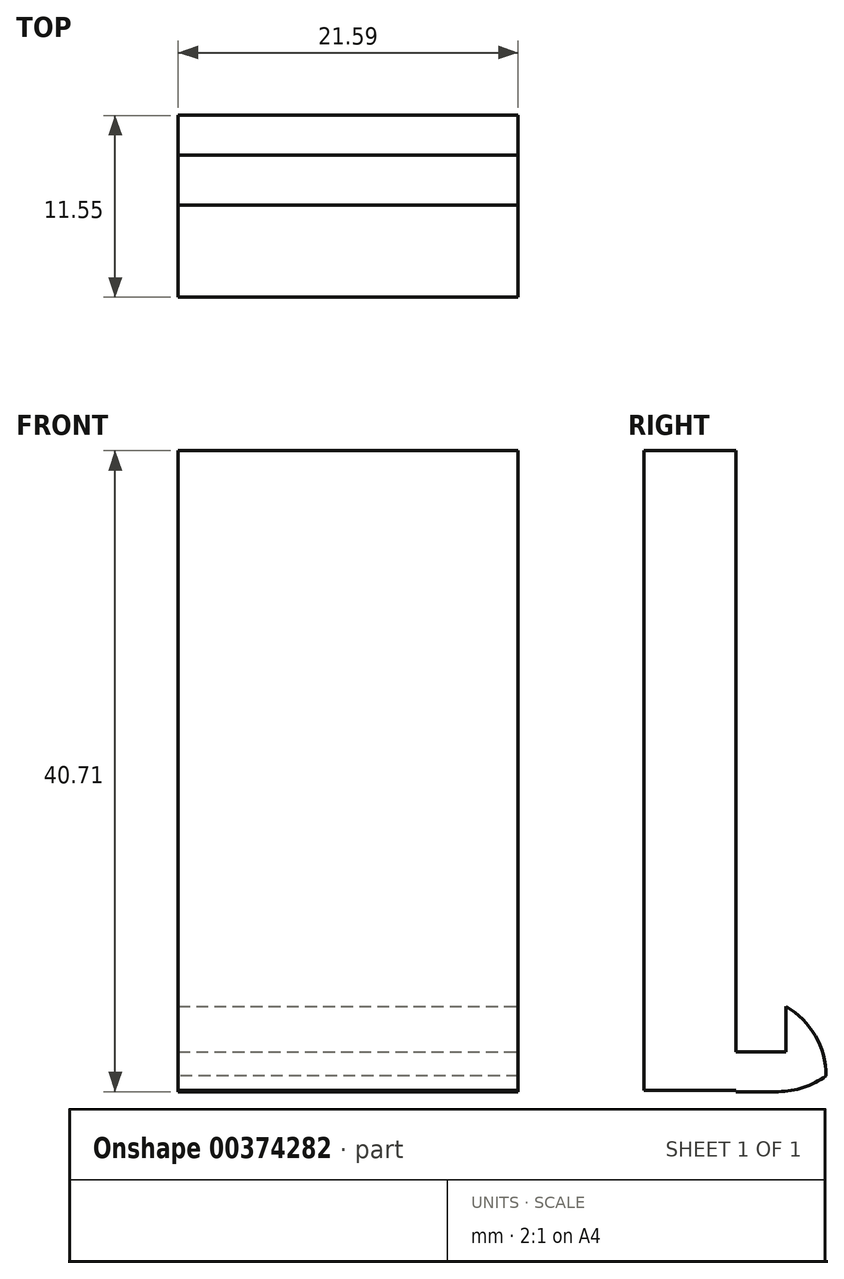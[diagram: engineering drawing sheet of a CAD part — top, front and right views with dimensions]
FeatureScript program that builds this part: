
annotation { "Feature Type Name" : "Feature", "Feature Type Description" : "" }
export const myFeature = defineFeature(function(context is Context, id is Id, definition is map)
    precondition{}
    {
        {
            var Q0;
            Q0=qCreatedBy(makeId("Front.planeOp"),FACE);
            var sketch = newSketch(context, id + "F0", { "sketchPlane" : qUnion([Q0])});
            skLineSegment(sketch, "E0", {"start": v(0, 40.64) * mm, "end": v(0, 0) * mm});
            skLineSegment(sketch, "E1", {"start": v(0, 0) * mm, "end": v(-21.59, 0) * mm});
            skLineSegment(sketch, "E2", {"start": v(-21.59, 0) * mm, "end": v(-21.59, 40.64) * mm});
            skLineSegment(sketch, "E3", {"start": v(-21.59, 40.64) * mm, "end": v(0, 40.64) * mm});
            skSolve(sketch);
        }
        {
            var Q0;
            Q0 = qSketchRegion(id + "F0", true);
            extrude(context, id + "F1", {"entities" : qUnion([Q0]), "depth" : 5.84 * mm});
        }
        {
            var Q0;
            Q0=qCreatedBy(makeId("Right.planeOp"),FACE);
            var sketch = newSketch(context, id + "F2", { "sketchPlane" : qUnion([Q0])});
            skLineSegment(sketch, "E4", {"start": v(5.72, 5.34) * mm, "end": v(5.72, 2.47) * mm});
            skLineSegment(sketch, "E5", {"start": v(5.72, 5.34) * mm, "end": v(3.18, 5.34) * mm});
            skLineSegment(sketch, "E6", {"start": v(3.18, -0.07) * mm, "end": v(0, -0.07) * mm});
            skLineSegment(sketch, "E7", {"start": v(0, 2.47) * mm, "end": v(0, -0.07) * mm});
            skLineSegment(sketch, "E8", {"start": v(0, 2.47) * mm, "end": v(3.18, 2.47) * mm});
            skLineSegment(sketch, "E9", {"start": v(3.17, -0.07) * mm, "end": v(5.72, 0) * mm});
            skLineSegment(sketch, "E10", {"start": v(5.72, 0) * mm, "end": v(5.72, 2.47) * mm});
            skLineSegment(sketch, "E11", {"start": v(3.18, 5.34) * mm, "end": v(3.18, 2.47) * mm});
            skSolve(sketch);
        }
        {
            var Q0;
            Q0 = qSketchRegion(id + "F2", true);
            extrude(context, id + "F3", {"entities" : qUnion([Q0]), "operationType" : NewBodyOperationType.ADD, "oppositeDirection" : true, "depth" : 21.59 * mm});
        }
        {
            var Q0;
            Q0=makeQuery(id+"F3.opExtrude","SWEPT_EDGE",EDGE,{"disambiguationData":[OSD([sQuery(id+"F2.wireOp",EDGE,"OhWGgMoe-Sf9Y-OSFl-5fwh-dTATBduO0PpF"),sQuery(id+"F2.wireOp",EDGE,"E4")])]});
            fillet(context, id + "F4", {"entities" : qUnion([Q0]), "radius" : 5.08 * mm, "tangentPropagation" : true, "allowEdgeOverflow" : false});
        }
        {
            var Q0;
            Q0=makeQuery(id+"F3.opExtrude","SWEPT_EDGE",EDGE,{"disambiguationData":[OSD([sQuery(id+"F2.wireOp",EDGE,"E9"),sQuery(id+"F2.wireOp",EDGE,"E10")])]});
            var Q1;
            {var subQ0=sQuery(id+"F2.wireOp",EDGE,"E4");Q1=makeQuery(id+"F4.opFillet","BLEND_EDGE",EDGE,{"blendedFrom":[makeQuery(id+"F3.opExtrude","SWEPT_EDGE",EDGE,{"disambiguationData":[OSD([subQ0,sQuery(id+"F2.wireOp",EDGE,"E5")])]}),makeQuery(id+"F3.opExtrude","SWEPT_FACE",FACE,{"disambiguationData":[OSD([subQ0,sQuery(id+"F2.wireOp",EDGE,"E10")])]})],"blendedInto":[makeQuery(id+"F3.opExtrude","SWEPT_FACE",FACE,{"disambiguationData":[OSD([subQ0,sQuery(id+"F2.wireOp",EDGE,"E10")])]})]});}
            fillet(context, id + "F5", {"entities" : qUnion([Q0, Q1]), "radius" : 5.08 * mm, "tangentPropagation" : true, "allowEdgeOverflow" : false});
        }
    });
